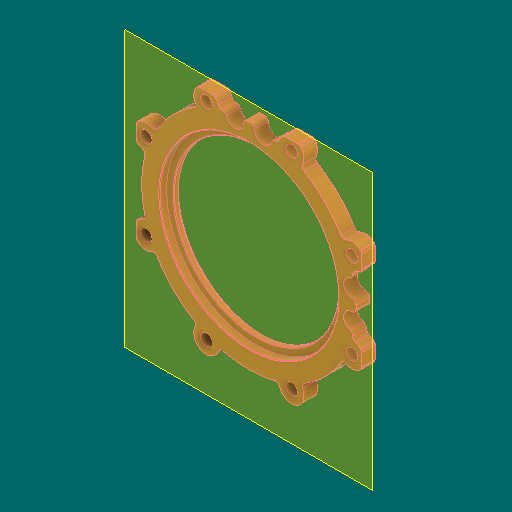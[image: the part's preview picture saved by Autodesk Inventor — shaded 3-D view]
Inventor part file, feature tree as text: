
AUTODESK INVENTOR PART (.ipt)
format: ipt  version: 2023.1 (Build 271208000, 208)  size: 339,456 bytes
history: native  units: in
note: dims shown in document units (in); Inventor stores cm internally (conversion verified against a paired STEP export)
features: other x3, sketch x2, plane x1
ambient origin geometry x8: Origin, YZ Plane, XZ Plane, XY Plane, X Axis, Y Axis, Z Axis, Center Point
bodies: Solid1 (feature_tree)
feature tree (6):
  other  "UpperRaceRing.ipt"
  other  "Solid1::UpperRaceRing.ipt"
  other  "TaggingFeature1"
  sketch  "Sketch1"  dims[d0=0.3937in]
  sketch  "Sketch2"
  plane  "Work Plane1"
